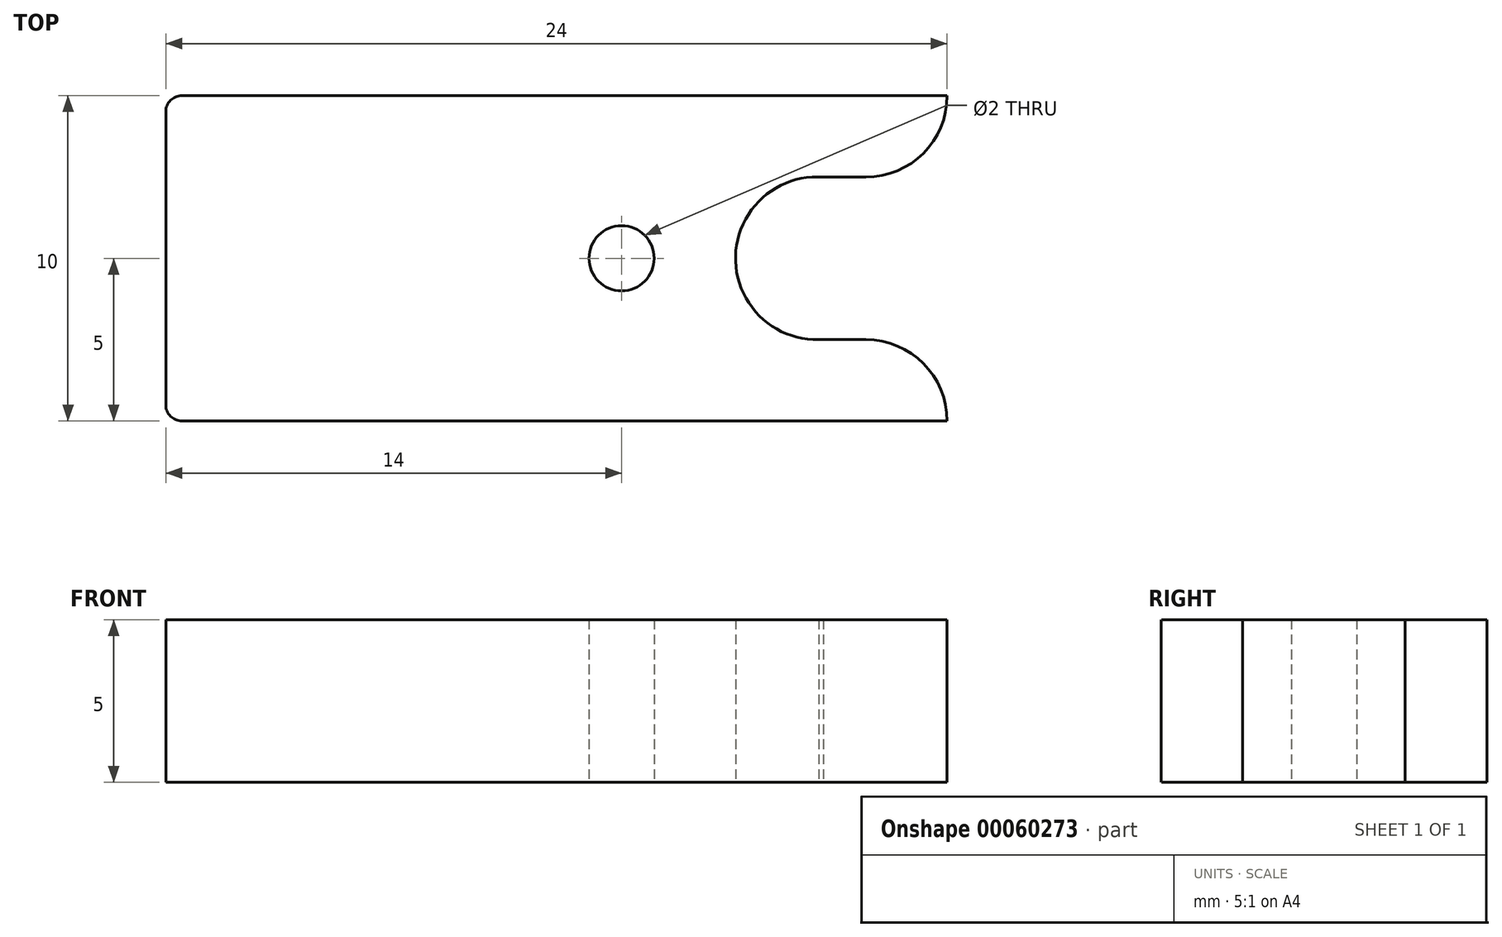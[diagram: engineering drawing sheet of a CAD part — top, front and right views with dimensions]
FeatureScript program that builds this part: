
annotation { "Feature Type Name" : "Feature", "Feature Type Description" : "" }
export const myFeature = defineFeature(function(context is Context, id is Id, definition is map)
    precondition{}
    {
        {
            var Q0;
            Q0=qCreatedBy(makeId("Top.planeOp"),FACE);
            var sketch = newSketch(context, id + "F0", { "sketchPlane" : qUnion([Q0])});
            skLineSegment(sketch, "E0.bottom", {"start": v(0.5, 0) * mm, "end": v(24, 0) * mm});
            skLineSegment(sketch, "E0.top", {"start": v(0.5, -10) * mm, "end": v(24, -10) * mm});
            skLineSegment(sketch, "E0.left", {"start": v(0, -0.5) * mm, "end": v(0, -9.5) * mm});
            skLineSegment(sketch, "E1", {"start": v(0, -5) * mm, "end": v(24, -5) * mm, "construction": true});
            skCircle(sketch, "E2", {"center": v(14, -5) * mm, "radius": 1 * mm});
            skArc(sketch, "E3", {"start": v(20.2, -2.5) * mm, "mid": v(17.5, -4.93) * mm, "end": v(20.05, -7.5) * mm});
            skLineSegment(sketch, "E4", {"start": v(20.05, -7.5) * mm, "end": v(21.5, -7.5) * mm});
            skLineSegment(sketch, "E5", {"start": v(19.8, -2.5) * mm, "end": v(21.5, -2.5) * mm});
            skLineSegment(sketch, "E6", {"start": v(24, -10) * mm, "end": v(24, -10) * mm});
            skLineSegment(sketch, "E7", {"start": v(24, 0) * mm, "end": v(24, 0) * mm});
            skArc(sketch, "E8.filletArc", {"start": v(24, -10) * mm, "mid": v(23.27, -8.23) * mm, "end": v(21.5, -7.5) * mm});
            skArc(sketch, "E9.filletArc", {"start": v(21.5, -2.5) * mm, "mid": v(23.27, -1.78) * mm, "end": v(24, 0) * mm});
            skPoint(sketch, "E10.visualSharp", {"position": v(0, 0) * mm});
            skArc(sketch, "E10.filletArc", {"start": v(0.5, 0) * mm, "mid": v(0.15, -0.15) * mm, "end": v(0, -0.5) * mm});
            skPoint(sketch, "E11.visualSharp", {"position": v(0, -10) * mm});
            skArc(sketch, "E11.filletArc", {"start": v(0, -9.5) * mm, "mid": v(0.15, -9.85) * mm, "end": v(0.5, -10) * mm});
            skSolve(sketch);
        }
        {
            var Q0;
            Q0=makeQuery(id+"F0.imprint","IMPRINT",FACE,{"disambiguationData":[TD([[makeQuery(id+"F0.imprint","IMPRINT",EDGE,{"derivedFrom":sQuery(id+"F0.wireOp",EDGE,"E0.bottom")}),-1.0]])]});
            extrude(context, id + "F1", {"entities" : qUnion([Q0]), "depth" : 5 * mm});
        }
    });
